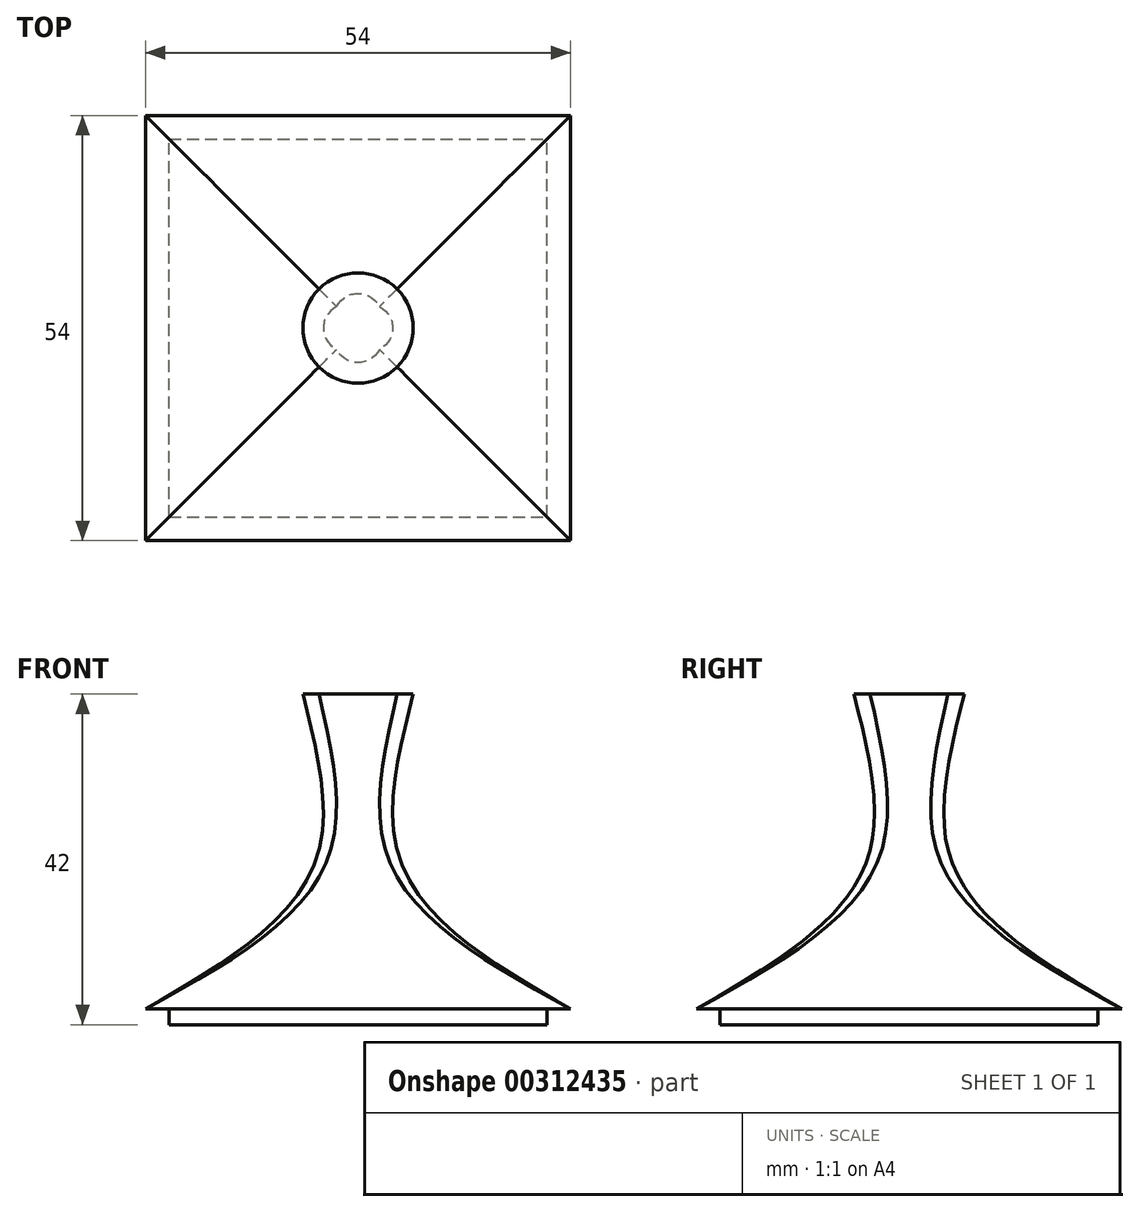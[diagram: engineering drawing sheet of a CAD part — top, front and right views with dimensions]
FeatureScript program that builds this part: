
annotation { "Feature Type Name" : "Feature", "Feature Type Description" : "" }
export const myFeature = defineFeature(function(context is Context, id is Id, definition is map)
    precondition{}
    {
        {
            var Q0;
            Q0=qCreatedBy(makeId("Top.planeOp"),FACE);
            var sketch = newSketch(context, id + "F0", { "sketchPlane" : qUnion([Q0])});
            skLineSegment(sketch, "E0.bottom", {"start": v(-27, -27) * mm, "end": v(27, -27) * mm});
            skLineSegment(sketch, "E0.top", {"start": v(-27, 27) * mm, "end": v(27, 27) * mm});
            skLineSegment(sketch, "E0.left", {"start": v(-27, -27) * mm, "end": v(-27, 27) * mm});
            skLineSegment(sketch, "E0.right", {"start": v(27, -27) * mm, "end": v(27, 27) * mm});
            skPoint(sketch, "E0.middle", {"position": v(0, 0) * mm});
            skSolve(sketch);
        }
        {
            var Q0;
            Q0=qCreatedBy(makeId("Top.planeOp"),FACE);
            cPlane(context, id + "F1", {"entities" : qUnion([Q0]), "cplaneType" : CPlaneType.OFFSET, "offset" : 20 * mm, "width" : 150 * mm, "height" : 150 * mm});
        }
        {
            var Q0;
            Q0=qCreatedBy(id+"F1.planeOp",FACE);
            var sketch = newSketch(context, id + "F2", { "sketchPlane" : qUnion([Q0])});
            skCircle(sketch, "E1", {"center": v(0, 0) * mm, "radius": 5 * mm});
            skSolve(sketch);
        }
        {
            var Q0;
            Q0=qCreatedBy(id+"F1.planeOp",FACE);
            cPlane(context, id + "F3", {"entities" : qUnion([Q0]), "cplaneType" : CPlaneType.OFFSET, "offset" : 20 * mm, "width" : 150 * mm, "height" : 150 * mm});
        }
        {
            var Q0;
            Q0=qCreatedBy(id+"F3.planeOp",FACE);
            var sketch = newSketch(context, id + "F4", { "sketchPlane" : qUnion([Q0])});
            skCircle(sketch, "E2", {"center": v(0, 0) * mm, "radius": 7 * mm});
            skSolve(sketch);
        }
        {
            var Q0;
            Q0=makeQuery(id+"F0.imprint","IMPRINT",FACE,{"disambiguationData":[TD([[makeQuery(id+"F0.imprint","IMPRINT",EDGE,{"derivedFrom":sQuery(id+"F0.wireOp",EDGE,"E0.bottom")}),1.0]])]});
            var Q1;
            Q1=makeQuery(id+"F2.imprint","IMPRINT",FACE,{"disambiguationData":[TD([[makeQuery(id+"F2.imprint","IMPRINT",EDGE,{"derivedFrom":sQuery(id+"F2.wireOp",EDGE,"E1")}),1.0]])]});
            var Q2;
            Q2=makeQuery(id+"F4.imprint","IMPRINT",FACE,{"disambiguationData":[TD([[makeQuery(id+"F4.imprint","IMPRINT",EDGE,{"derivedFrom":sQuery(id+"F4.wireOp",EDGE,"E2")}),1.0]])]});
            loft(context, id + "F5", {"sheetProfilesArray" : [{ "sheetProfileEntities" : qUnion([Q0]) }, { "sheetProfileEntities" : qUnion([Q1]) }, { "sheetProfileEntities" : qUnion([Q2]) }]});
        }
        {
            var Q0;
            Q0=qCreatedBy(makeId("Top.planeOp"),FACE);
            var sketch = newSketch(context, id + "F6", { "sketchPlane" : qUnion([Q0])});
            skLineSegment(sketch, "E3.bottom", {"start": v(-24, -24) * mm, "end": v(24, -24) * mm});
            skLineSegment(sketch, "E3.top", {"start": v(-24, 24) * mm, "end": v(24, 24) * mm});
            skLineSegment(sketch, "E3.left", {"start": v(-24, -24) * mm, "end": v(-24, 24) * mm});
            skLineSegment(sketch, "E3.right", {"start": v(24, -24) * mm, "end": v(24, 24) * mm});
            skPoint(sketch, "E3.middle", {"position": v(0, 0) * mm});
            skSolve(sketch);
        }
        {
            var Q0;
            Q0=makeQuery(id+"F6.imprint","IMPRINT",FACE,{"disambiguationData":[TD([[makeQuery(id+"F6.imprint","IMPRINT",EDGE,{"derivedFrom":sQuery(id+"F6.wireOp",EDGE,"E3.bottom")}),1.0]])]});
            extrude(context, id + "F7", {"entities" : qUnion([Q0]), "operationType" : NewBodyOperationType.ADD, "oppositeDirection" : true, "depth" : 2 * mm});
        }
    });
